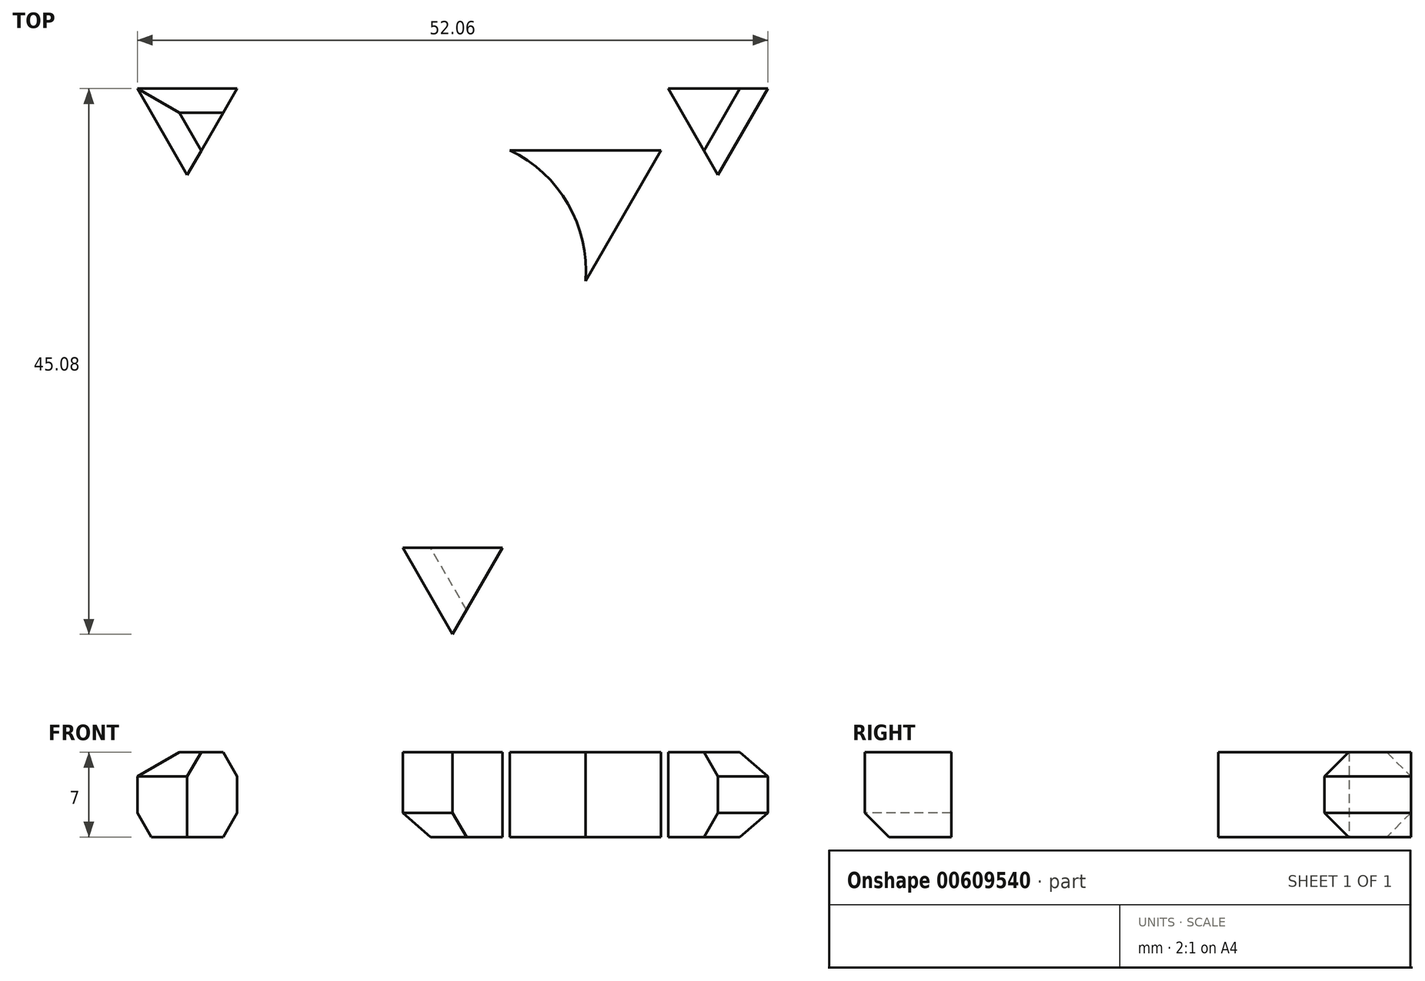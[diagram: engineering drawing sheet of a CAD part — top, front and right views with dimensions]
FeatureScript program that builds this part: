
annotation { "Feature Type Name" : "Feature", "Feature Type Description" : "" }
export const myFeature = defineFeature(function(context is Context, id is Id, definition is map)
    precondition{}
    {
        {
            var Q0;
            Q0=qCreatedBy(makeId("Top.planeOp"),FACE);
            var sketch = newSketch(context, id + "F0", { "sketchPlane" : qUnion([Q0])});
            skCircle(sketch, "E0", {"center": v(0, 0) * mm, "radius": 11 * mm});
            skCircle(sketch, "E1.cCircle", {"center": v(0, 0) * mm, "radius": 11 * mm, "construction": true});
            skLineSegment(sketch, "E2.0", {"start": v(-17.2, 9.93) * mm, "end": v(17.2, 9.93) * mm});
            skLineSegment(sketch, "E2.1", {"start": v(17.2, 9.93) * mm, "end": v(0, -19.86) * mm});
            skLineSegment(sketch, "E2.2", {"start": v(0, -19.86) * mm, "end": v(-17.2, 9.93) * mm});
            skPoint(sketch, "E2.0.midPoint", {"position": v(0, 9.93) * mm});
            skLineSegment(sketch, "E3.0", {"start": v(-26.03, 15.03) * mm, "end": v(26.03, 15.03) * mm});
            skLineSegment(sketch, "E3.1", {"start": v(26.03, 15.03) * mm, "end": v(0, -30.05) * mm});
            skLineSegment(sketch, "E3.2", {"start": v(0, -30.05) * mm, "end": v(-26.03, 15.03) * mm});
            skPoint(sketch, "E3.0.midPoint", {"position": v(0, 15.03) * mm});
            skCircle(sketch, "E4.cCircle", {"center": v(0, 0) * mm, "radius": 22.92 * mm, "construction": true});
            skLineSegment(sketch, "E4.0", {"start": v(-13.23, 22.92) * mm, "end": v(13.23, 22.92) * mm});
            skLineSegment(sketch, "E4.1", {"start": v(13.23, 22.92) * mm, "end": v(26.46, 0) * mm});
            skLineSegment(sketch, "E4.2", {"start": v(26.46, 0) * mm, "end": v(13.23, -22.92) * mm});
            skLineSegment(sketch, "E4.3", {"start": v(13.23, -22.92) * mm, "end": v(-13.23, -22.92) * mm});
            skLineSegment(sketch, "E4.4", {"start": v(-13.23, -22.92) * mm, "end": v(-26.46, 0) * mm});
            skLineSegment(sketch, "E4.5", {"start": v(-26.46, 0) * mm, "end": v(-13.23, 22.92) * mm});
            skPoint(sketch, "E4.0.midPoint", {"position": v(0, 22.92) * mm});
            skCircle(sketch, "E5", {"center": v(0, 22.92) * mm, "radius": 9.5 * mm});
            skCircle(sketch, "E6", {"center": v(19.85, -11.46) * mm, "radius": 9.5 * mm});
            skCircle(sketch, "E7", {"center": v(-19.85, -11.46) * mm, "radius": 9.5 * mm});
            skSolve(sketch);
        }
        {
            var Q0;
            {var subQ6=sQuery(id+"F0.wireOp",EDGE,"E2.0");var subQ8=sQuery(id+"F0.wireOp",EDGE,"E0");var subQ21=makeQuery(id+"F0.imprint","INTERSECT",VERTEX,{"disambiguationData":[OD(0.0)],"derivedFrom":[subQ8,subQ6]});Q0=makeQuery(id+"F0.imprint","IMPRINT",FACE,{"disambiguationData":[TD([[makeQuery(id+"F0.imprint","IMPRINT",EDGE,{"disambiguationData":[TD([[subQ21,1.0]])],"derivedFrom":subQ8}),-1.0]])]});}
            var Q1;
            {var subQ0=sQuery(id+"F0.wireOp",EDGE,"E3.2");var subQ1=sQuery(id+"F0.wireOp",EDGE,"E3.0");var subQ2=makeQuery(id+"F0.imprint","INTERSECT",VERTEX,{"derivedFrom":[subQ1,subQ0]});Q1=makeQuery(id+"F0.imprint","IMPRINT",FACE,{"disambiguationData":[TD([[makeQuery(id+"F0.imprint","IMPRINT",EDGE,{"disambiguationData":[TD([[subQ2,-1.0]])],"derivedFrom":subQ1}),-1.0]])]});}
            var Q2;
            {var subQ0=sQuery(id+"F0.wireOp",EDGE,"E3.1");var subQ1=sQuery(id+"F0.wireOp",EDGE,"E3.0");var subQ2=makeQuery(id+"F0.imprint","INTERSECT",VERTEX,{"derivedFrom":[subQ1,subQ0]});Q2=makeQuery(id+"F0.imprint","IMPRINT",FACE,{"disambiguationData":[TD([[makeQuery(id+"F0.imprint","IMPRINT",EDGE,{"disambiguationData":[TD([[subQ2,1.0]])],"derivedFrom":subQ1}),-1.0]])]});}
            var Q3;
            {var subQ0=sQuery(id+"F0.wireOp",EDGE,"E3.2");var subQ1=sQuery(id+"F0.wireOp",EDGE,"E3.1");var subQ2=makeQuery(id+"F0.imprint","INTERSECT",VERTEX,{"derivedFrom":[subQ1,subQ0]});Q3=makeQuery(id+"F0.imprint","IMPRINT",FACE,{"disambiguationData":[TD([[makeQuery(id+"F0.imprint","IMPRINT",EDGE,{"disambiguationData":[TD([[subQ2,1.0]])],"derivedFrom":subQ1}),-1.0]])]});}
            extrude(context, id + "F1", {"entities" : qUnion([Q0, Q1, Q2, Q3]), "depth" : 7 * mm, "offsetDistance" : 25.4 * mm});
        }
        {
            var Q0;
            {var subQ0=sQuery(id+"F0.wireOp",EDGE,"E3.2");var subQ1=makeQuery(id+"F0.imprint","INTERSECT",VERTEX,{"derivedFrom":[subQ0,sQuery(id+"F0.wireOp",EDGE,"E4.5")]});Q0=makeQuery(id+"F1.opExtrude","CAP_EDGE",EDGE,{"disambiguationData":[OSD([subQ0]),TDD([makeQuery(id+"F0.imprint","IMPRINT",EDGE,{"disambiguationData":[TD([[subQ1,1.0]])],"derivedFrom":subQ0}),makeQuery(id+"F0.imprint","IMPRINT",EDGE,{"disambiguationData":[TD([[makeQuery(id+"F0.imprint","INTERSECT",VERTEX,{"derivedFrom":[sQuery(id+"F0.wireOp",EDGE,"E3.0"),subQ0]}),1.0]])],"derivedFrom":subQ0})])],"isStart":false});}
            var Q1;
            {var subQ0=sQuery(id+"F0.wireOp",EDGE,"E3.2");var subQ1=makeQuery(id+"F0.imprint","INTERSECT",VERTEX,{"derivedFrom":[subQ0,sQuery(id+"F0.wireOp",EDGE,"E4.3")]});Q1=makeQuery(id+"F1.opExtrude","CAP_EDGE",EDGE,{"disambiguationData":[OSD([subQ0]),TDD([makeQuery(id+"F0.imprint","IMPRINT",EDGE,{"disambiguationData":[TD([[makeQuery(id+"F0.imprint","INTERSECT",VERTEX,{"derivedFrom":[sQuery(id+"F0.wireOp",EDGE,"E3.1"),subQ0]}),-1.0]])],"derivedFrom":subQ0}),makeQuery(id+"F0.imprint","IMPRINT",EDGE,{"disambiguationData":[TD([[subQ1,-1.0]])],"derivedFrom":subQ0})])],"isStart":true});}
            var Q2;
            {var subQ0=sQuery(id+"F0.wireOp",EDGE,"E3.0");var subQ1=makeQuery(id+"F0.imprint","INTERSECT",VERTEX,{"derivedFrom":[subQ0,sQuery(id+"F0.wireOp",EDGE,"E4.5")]});Q2=makeQuery(id+"F1.opExtrude","CAP_EDGE",EDGE,{"disambiguationData":[OSD([subQ0]),TDD([makeQuery(id+"F0.imprint","IMPRINT",EDGE,{"disambiguationData":[TD([[makeQuery(id+"F0.imprint","INTERSECT",VERTEX,{"derivedFrom":[subQ0,sQuery(id+"F0.wireOp",EDGE,"E3.2")]}),-1.0]])],"derivedFrom":subQ0}),makeQuery(id+"F0.imprint","IMPRINT",EDGE,{"disambiguationData":[TD([[subQ1,-1.0]])],"derivedFrom":subQ0})])],"isStart":false});}
            var Q3;
            {var subQ0=sQuery(id+"F0.wireOp",EDGE,"E3.0");var subQ1=makeQuery(id+"F0.imprint","INTERSECT",VERTEX,{"derivedFrom":[subQ0,sQuery(id+"F0.wireOp",EDGE,"E4.5")]});Q3=makeQuery(id+"F1.opExtrude","CAP_EDGE",EDGE,{"disambiguationData":[OSD([subQ0]),TDD([makeQuery(id+"F0.imprint","IMPRINT",EDGE,{"disambiguationData":[TD([[makeQuery(id+"F0.imprint","INTERSECT",VERTEX,{"derivedFrom":[subQ0,sQuery(id+"F0.wireOp",EDGE,"E3.2")]}),-1.0]])],"derivedFrom":subQ0}),makeQuery(id+"F0.imprint","IMPRINT",EDGE,{"disambiguationData":[TD([[subQ1,-1.0]])],"derivedFrom":subQ0})])],"isStart":true});}
            var Q4;
            {var subQ0=sQuery(id+"F0.wireOp",EDGE,"E3.1");var subQ1=makeQuery(id+"F0.imprint","INTERSECT",VERTEX,{"derivedFrom":[subQ0,sQuery(id+"F0.wireOp",EDGE,"E4.1")]});Q4=makeQuery(id+"F1.opExtrude","CAP_EDGE",EDGE,{"disambiguationData":[OSD([subQ0]),TDD([makeQuery(id+"F0.imprint","IMPRINT",EDGE,{"disambiguationData":[TD([[makeQuery(id+"F0.imprint","INTERSECT",VERTEX,{"derivedFrom":[sQuery(id+"F0.wireOp",EDGE,"E3.0"),subQ0]}),-1.0]])],"derivedFrom":subQ0}),makeQuery(id+"F0.imprint","IMPRINT",EDGE,{"disambiguationData":[TD([[subQ1,-1.0]])],"derivedFrom":subQ0})])],"isStart":false});}
            var Q5;
            {var subQ0=sQuery(id+"F0.wireOp",EDGE,"E3.1");var subQ1=makeQuery(id+"F0.imprint","INTERSECT",VERTEX,{"derivedFrom":[subQ0,sQuery(id+"F0.wireOp",EDGE,"E4.1")]});Q5=makeQuery(id+"F1.opExtrude","CAP_EDGE",EDGE,{"disambiguationData":[OSD([subQ0]),TDD([makeQuery(id+"F0.imprint","IMPRINT",EDGE,{"disambiguationData":[TD([[makeQuery(id+"F0.imprint","INTERSECT",VERTEX,{"derivedFrom":[sQuery(id+"F0.wireOp",EDGE,"E3.0"),subQ0]}),-1.0]])],"derivedFrom":subQ0}),makeQuery(id+"F0.imprint","IMPRINT",EDGE,{"disambiguationData":[TD([[subQ1,-1.0]])],"derivedFrom":subQ0})])],"isStart":true});}
            chamfer(context, id + "F2", {"entities" : qUnion([Q0, Q1, Q2, Q3, Q4, Q5]), "width" : 2 * mm, "tangentPropagation" : true});
        }
    });
